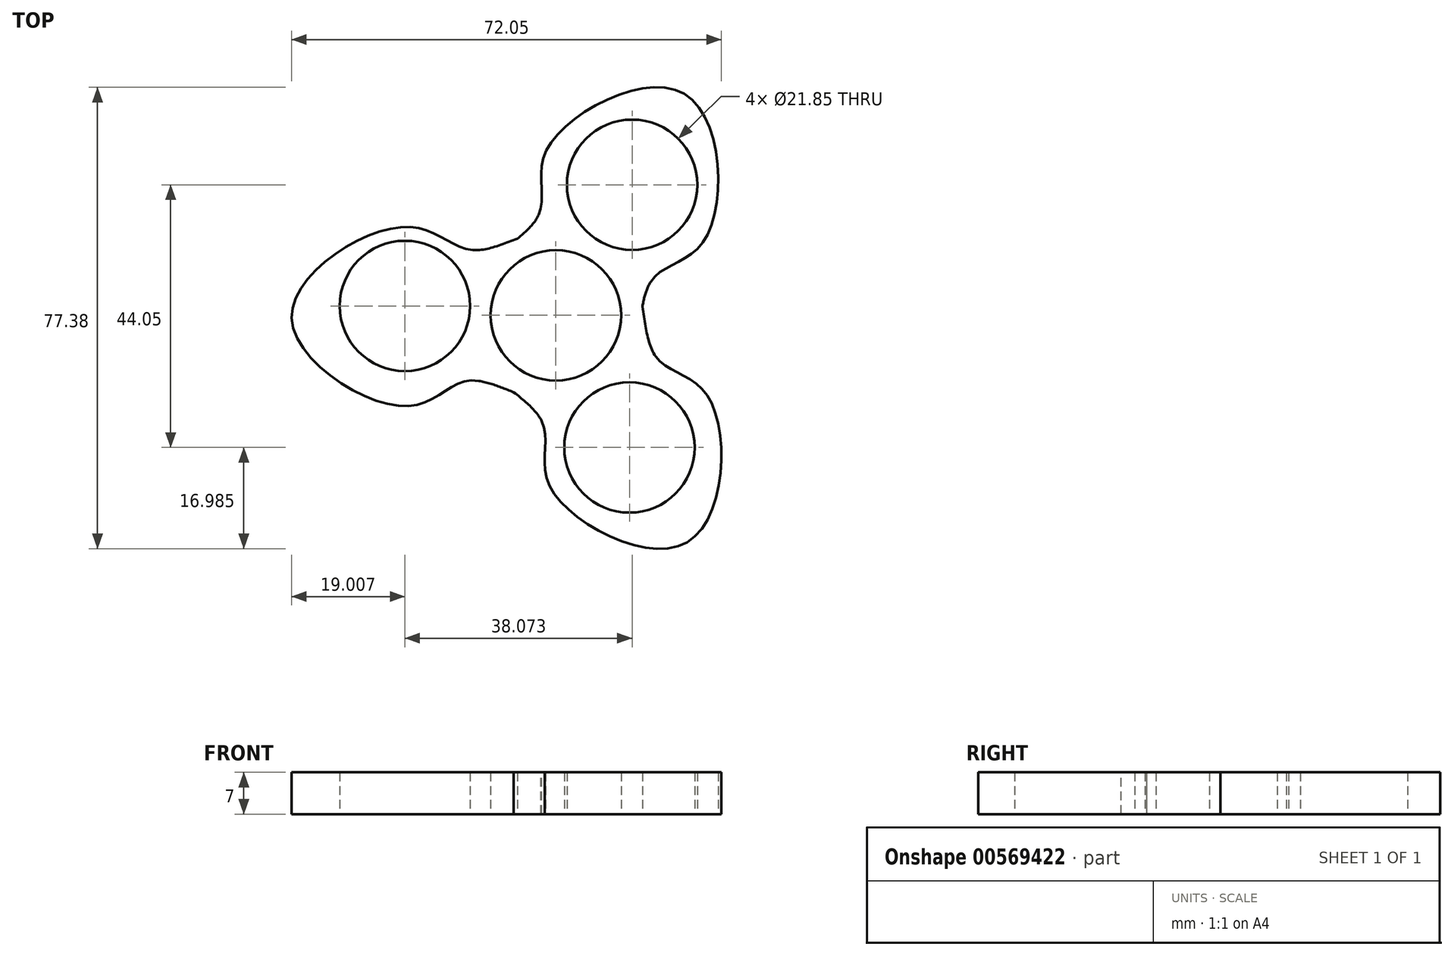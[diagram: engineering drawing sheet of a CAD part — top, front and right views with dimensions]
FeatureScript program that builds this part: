
annotation { "Feature Type Name" : "Feature", "Feature Type Description" : "" }
export const myFeature = defineFeature(function(context is Context, id is Id, definition is map)
    precondition{}
    {
        {
            var Q0;
            Q0=qCreatedBy(makeId("Top.planeOp"),FACE);
            var sketch = newSketch(context, id + "F0", { "sketchPlane" : qUnion([Q0])});
            skPoint(sketch, "E0.middle", {"position": v(0.02, 0.4) * mm});
            skCircle(sketch, "E1", {"center": v(0.02, 0.4) * mm, "radius": 10.93 * mm});
            skPoint(sketch, "E2", {"position": v(0.42, 10.88) * mm});
            skLineSegment(sketch, "E3", {"start": v(0.42, 10.88) * mm, "end": v(0.05, 10.89) * mm, "construction": true});
            skPoint(sketch, "E4", {"position": v(-13.95, 11.35) * mm});
            skFitSpline(sketch, "E5", {"points": [v(0.1, 14.76) * mm, v(-13.95, 11.35) * mm, v(-25.02, 15.24) * mm, v(-44.3, 0) * mm], "startDerivative": vector(-45.32, 0.62) * mm, "endDerivative": vector(0.12, -55.35) * mm});
            skCircle(sketch, "E6", {"center": v(-25.28, 1.98) * mm, "radius": 10.93 * mm});
            skCircle(sketch, "E7.1.0", {"center": v(12.34, -21.75) * mm, "radius": 10.93 * mm});
            skCircle(sketch, "E7.2.0", {"center": v(12.8, 22.3) * mm, "radius": 10.93 * mm});
            skPoint(sketch, "E7.center", {"position": v(0, 0) * mm});
            skFitSpline(sketch, "E8", {"points": [v(0.15, -14.36) * mm, v(-14.5, -10.55) * mm, v(-24.98, -14.84) * mm, v(-44.3, 0.4) * mm], "startDerivative": vector(-45.32, -0.62) * mm, "endDerivative": vector(0.12, 55.35) * mm});
            skFitSpline(sketch, "E9", {"points": [v(12.05, -8.32) * mm, v(16.08, 6.28) * mm, v(25.02, 13.2) * mm, v(21.5, 37.56) * mm], "startDerivative": vector(23.2, 38.94) * mm, "endDerivative": vector(-48, 27.57) * mm});
            skFitSpline(sketch, "E10", {"points": [v(-13.52, 6.44) * mm, v(-2.9, 17.23) * mm, v(-1.37, 28.44) * mm, v(21.5, 37.56) * mm], "startDerivative": vector(22.13, 39.56) * mm, "endDerivative": vector(47.88, -27.78) * mm});
            skFitSpline(sketch, "E11", {"points": [v(-12.93, -6.66) * mm, v(-2.3, -17.45) * mm, v(-0.78, -28.66) * mm, v(21.99, -37.65) * mm], "startDerivative": vector(22.13, -39.56) * mm, "endDerivative": vector(47.88, 27.78) * mm});
            skFitSpline(sketch, "E12", {"points": [v(12.64, 8.1) * mm, v(16.73, -6.47) * mm, v(25.62, -13.42) * mm, v(21.99, -37.65) * mm], "startDerivative": vector(23.2, -38.94) * mm, "endDerivative": vector(-48, -27.57) * mm});
            skLineSegment(sketch, "E13", {"start": v(-13.95, 11.35) * mm, "end": v(-2.9, 17.23) * mm});
            skLineSegment(sketch, "E14", {"start": v(15.9, 6.03) * mm, "end": v(16.73, -6.47) * mm});
            skLineSegment(sketch, "E15", {"start": v(-2.34, -17.36) * mm, "end": v(-12.89, -10.6) * mm});
            skCircle(sketch, "E16", {"center": v(0.02, 0.4) * mm, "radius": 44.31 * mm});
            skSolve(sketch);
        }
        {
            var Q0;
            Q0=makeQuery(id+"F0.imprint","IMPRINT",FACE,{"disambiguationData":[TD([[makeQuery(id+"F0.imprint","IMPRINT",EDGE,{"derivedFrom":sQuery(id+"F0.wireOp",EDGE,"E1")}),-1.0]])]});
            extrude(context, id + "F1", {"entities" : qUnion([Q0]), "depth" : 7 * mm, "offsetDistance" : 25 * mm});
        }
    });
